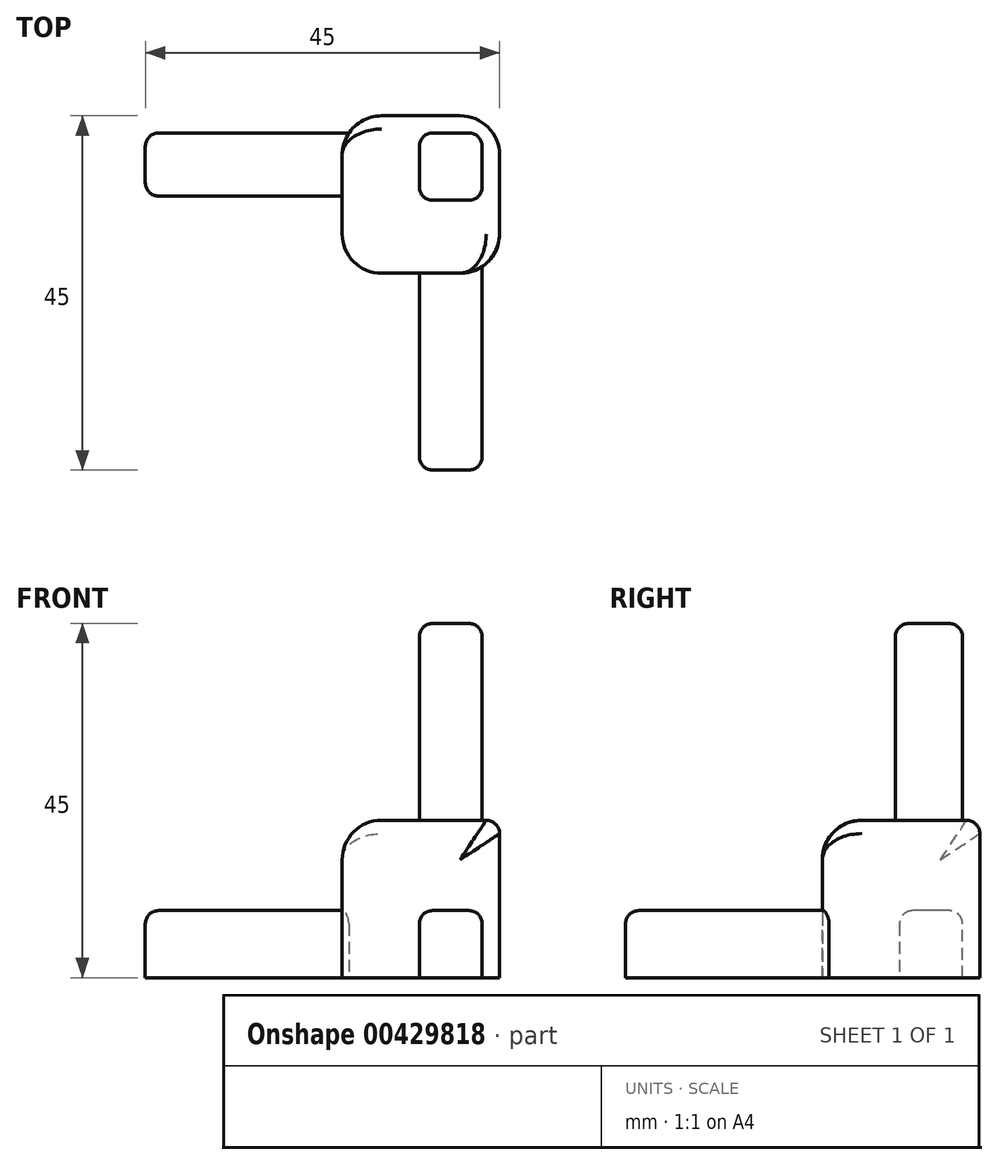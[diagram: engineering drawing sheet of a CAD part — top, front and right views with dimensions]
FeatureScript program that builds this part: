
annotation { "Feature Type Name" : "Feature", "Feature Type Description" : "" }
export const myFeature = defineFeature(function(context is Context, id is Id, definition is map)
    precondition{}
    {
        {
            var Q0;
            Q0=qCreatedBy(makeId("Front.planeOp"),FACE);
            var sketch = newSketch(context, id + "F0", { "sketchPlane" : qUnion([Q0])});
            skLineSegment(sketch, "E0.bottom", {"start": v(-6.86, 11.47) * mm, "end": v(13.14, 11.47) * mm});
            skLineSegment(sketch, "E0.top", {"start": v(-6.86, -8.53) * mm, "end": v(13.14, -8.53) * mm});
            skLineSegment(sketch, "E0.left", {"start": v(-6.86, 11.47) * mm, "end": v(-6.86, -8.53) * mm});
            skLineSegment(sketch, "E0.right", {"start": v(13.14, 11.47) * mm, "end": v(13.14, -8.53) * mm});
            skSolve(sketch);
        }
        {
            var Q0;
            Q0 = qSketchRegion(id + "F0", true);
            extrude(context, id + "F1", {"entities" : qUnion([Q0]), "depth" : 20 * mm});
        }
        {
            var Q0;
            Q0=makeQuery(id+"F1.opExtrude","SWEPT_FACE",FACE,{"disambiguationData":[OSD([sQuery(id+"F0.wireOp",EDGE,"E0.left")])]});
            var sketch = newSketch(context, id + "F2", { "sketchPlane" : qUnion([Q0])});
            skLineSegment(sketch, "E1", {"start": v(2.2, -8.53) * mm, "end": v(2.2, 0) * mm});
            skLineSegment(sketch, "E2", {"start": v(2.2, 0) * mm, "end": v(10.2, 0) * mm});
            skLineSegment(sketch, "E3", {"start": v(10.2, 0) * mm, "end": v(10.2, -8.53) * mm});
            skLineSegment(sketch, "E4", {"start": v(10.2, -8.53) * mm, "end": v(2.2, -8.53) * mm});
            skSolve(sketch);
        }
        {
            var Q0;
            Q0 = qSketchRegion(id + "F2", true);
            extrude(context, id + "F3", {"entities" : qUnion([Q0]), "operationType" : NewBodyOperationType.ADD, "depth" : 25 * mm});
        }
        {
            var Q0;
            Q0=makeQuery(id+"F1.opExtrude","CAP_FACE",FACE,{"disambiguationData":[OSD([sQuery(id+"F0.wireOp",EDGE,"E0.bottom"),sQuery(id+"F0.wireOp",EDGE,"E0.top"),sQuery(id+"F0.wireOp",EDGE,"E0.left"),sQuery(id+"F0.wireOp",EDGE,"E0.right")])],"isStart":false});
            var sketch = newSketch(context, id + "F4", { "sketchPlane" : qUnion([Q0])});
            skLineSegment(sketch, "E5.bottom", {"start": v(10.94, -8.53) * mm, "end": v(2.94, -8.53) * mm});
            skLineSegment(sketch, "E5.top", {"start": v(10.94, 0) * mm, "end": v(2.94, 0) * mm});
            skLineSegment(sketch, "E5.left", {"start": v(10.94, -8.53) * mm, "end": v(10.94, 0) * mm});
            skLineSegment(sketch, "E5.right", {"start": v(2.94, -8.53) * mm, "end": v(2.94, 0) * mm});
            skSolve(sketch);
        }
        {
            var Q0;
            Q0 = qSketchRegion(id + "F4", true);
            extrude(context, id + "F5", {"entities" : qUnion([Q0]), "operationType" : NewBodyOperationType.ADD, "depth" : 25 * mm});
        }
        {
            var Q0;
            Q0=makeQuery(id+"F1.opExtrude","SWEPT_FACE",FACE,{"disambiguationData":[OSD([sQuery(id+"F0.wireOp",EDGE,"E0.bottom")])]});
            var sketch = newSketch(context, id + "F6", { "sketchPlane" : qUnion([Q0])});
            skLineSegment(sketch, "E6", {"start": v(2.94, -2.2) * mm, "end": v(2.94, -10.73) * mm});
            skLineSegment(sketch, "E7", {"start": v(2.94, -10.73) * mm, "end": v(10.94, -10.73) * mm});
            skLineSegment(sketch, "E8", {"start": v(10.94, -10.73) * mm, "end": v(10.94, -2.2) * mm});
            skLineSegment(sketch, "E9", {"start": v(10.94, -2.2) * mm, "end": v(2.94, -2.2) * mm});
            skSolve(sketch);
        }
        {
            var Q0;
            Q0=makeQuery(id+"F6.imprint","IMPRINT",FACE,{"disambiguationData":[TD([[makeQuery(id+"F6.imprint","IMPRINT",EDGE,{"derivedFrom":sQuery(id+"F6.wireOp",EDGE,"E6")}),1.0]])]});
            extrude(context, id + "F7", {"entities" : qUnion([Q0]), "operationType" : NewBodyOperationType.ADD, "depth" : 25 * mm});
        }
        {
            var Q0;
            Q0=makeQuery(id+"F1.opExtrude","SWEPT_EDGE",EDGE,{"disambiguationData":[OSD([sQuery(id+"F0.wireOp",EDGE,"E0.bottom"),sQuery(id+"F0.wireOp",EDGE,"E0.left")])]});
            var Q1;
            Q1=makeQuery(id+"F1.opExtrude","CAP_EDGE",EDGE,{"disambiguationData":[OSD([sQuery(id+"F0.wireOp",EDGE,"E0.bottom")])],"isStart":false});
            var Q2;
            Q2=makeQuery(id+"F1.opExtrude","CAP_EDGE",EDGE,{"disambiguationData":[OSD([sQuery(id+"F0.wireOp",EDGE,"E0.left")])],"isStart":false});
            var Q3;
            Q3=makeQuery(id+"F1.opExtrude","CAP_EDGE",EDGE,{"disambiguationData":[OSD([sQuery(id+"F0.wireOp",EDGE,"E0.left")])],"isStart":true});
            var Q4;
            Q4=makeQuery(id+"F1.opExtrude","CAP_EDGE",EDGE,{"disambiguationData":[OSD([sQuery(id+"F0.wireOp",EDGE,"E0.right")])],"isStart":true});
            var Q5;
            Q5=makeQuery(id+"F1.opExtrude","CAP_EDGE",EDGE,{"disambiguationData":[OSD([sQuery(id+"F0.wireOp",EDGE,"E0.right")])],"isStart":false});
            fillet(context, id + "F8", {"entities" : qUnion([Q0, Q1, Q2, Q3, Q4, Q5]), "radius" : 5 * mm, "tangentPropagation" : true, "allowEdgeOverflow" : false});
        }
        {
            var Q0;
            Q0=makeQuery(id+"F3.opExtrude","CAP_EDGE",EDGE,{"disambiguationData":[OSD([sQuery(id+"F2.wireOp",EDGE,"E2")])],"isStart":false});
            var Q1;
            Q1=makeQuery(id+"F3.opExtrude","CAP_EDGE",EDGE,{"disambiguationData":[OSD([sQuery(id+"F2.wireOp",EDGE,"E3")])],"isStart":false});
            var Q2;
            Q2=makeQuery(id+"F3.opExtrude","SWEPT_EDGE",EDGE,{"disambiguationData":[OSD([sQuery(id+"F2.wireOp",EDGE,"E2"),sQuery(id+"F2.wireOp",EDGE,"E3")])]});
            var Q3;
            Q3=makeQuery(id+"F3.opExtrude","SWEPT_EDGE",EDGE,{"disambiguationData":[OSD([sQuery(id+"F2.wireOp",EDGE,"E1"),sQuery(id+"F2.wireOp",EDGE,"E2")])]});
            var Q4;
            Q4=makeQuery(id+"F5.opExtrude","SWEPT_EDGE",EDGE,{"disambiguationData":[OSD([sQuery(id+"F4.wireOp",EDGE,"E5.top"),sQuery(id+"F4.wireOp",EDGE,"E5.right")])]});
            var Q5;
            Q5=makeQuery(id+"F5.opExtrude","CAP_EDGE",EDGE,{"disambiguationData":[OSD([sQuery(id+"F4.wireOp",EDGE,"E5.right")])],"isStart":false});
            var Q6;
            Q6=makeQuery(id+"F5.opExtrude","CAP_EDGE",EDGE,{"disambiguationData":[OSD([sQuery(id+"F4.wireOp",EDGE,"E5.top")])],"isStart":false});
            var Q7;
            Q7=makeQuery(id+"F5.opExtrude","SWEPT_EDGE",EDGE,{"disambiguationData":[OSD([sQuery(id+"F4.wireOp",EDGE,"E5.top"),sQuery(id+"F4.wireOp",EDGE,"E5.left")])]});
            var Q8;
            Q8=makeQuery(id+"F3.opExtrude","CAP_EDGE",EDGE,{"disambiguationData":[OSD([sQuery(id+"F2.wireOp",EDGE,"E1")])],"isStart":false});
            var Q9;
            Q9=makeQuery(id+"F5.opExtrude","CAP_EDGE",EDGE,{"disambiguationData":[OSD([sQuery(id+"F4.wireOp",EDGE,"E5.left")])],"isStart":false});
            var Q10;
            Q10=makeQuery(id+"F7.opExtrude","SWEPT_EDGE",EDGE,{"disambiguationData":[OSD([sQuery(id+"F6.wireOp",EDGE,"E6"),sQuery(id+"F6.wireOp",EDGE,"E7")])]});
            var Q11;
            Q11=makeQuery(id+"F7.opExtrude","CAP_EDGE",EDGE,{"disambiguationData":[OSD([sQuery(id+"F6.wireOp",EDGE,"E6")])],"isStart":false});
            var Q12;
            Q12=makeQuery(id+"F7.opExtrude","CAP_EDGE",EDGE,{"disambiguationData":[OSD([sQuery(id+"F6.wireOp",EDGE,"E7")])],"isStart":false});
            var Q13;
            Q13=makeQuery(id+"F7.opExtrude","CAP_EDGE",EDGE,{"disambiguationData":[OSD([sQuery(id+"F6.wireOp",EDGE,"E9")])],"isStart":false});
            var Q14;
            Q14=makeQuery(id+"F7.opExtrude","CAP_EDGE",EDGE,{"disambiguationData":[OSD([sQuery(id+"F6.wireOp",EDGE,"E8")])],"isStart":false});
            var Q15;
            Q15=makeQuery(id+"F7.opExtrude","SWEPT_EDGE",EDGE,{"disambiguationData":[OSD([sQuery(id+"F6.wireOp",EDGE,"E8"),sQuery(id+"F6.wireOp",EDGE,"E9")])]});
            var Q16;
            Q16=makeQuery(id+"F1.opExtrude","CAP_EDGE",EDGE,{"disambiguationData":[OSD([sQuery(id+"F0.wireOp",EDGE,"E0.bottom")])],"isStart":true});
            var Q17;
            Q17=makeQuery(id+"F7.opExtrude","SWEPT_EDGE",EDGE,{"disambiguationData":[OSD([sQuery(id+"F6.wireOp",EDGE,"E6"),sQuery(id+"F6.wireOp",EDGE,"E9")])]});
            var Q18;
            Q18=makeQuery(id+"F7.opExtrude","SWEPT_EDGE",EDGE,{"disambiguationData":[OSD([sQuery(id+"F6.wireOp",EDGE,"E7"),sQuery(id+"F6.wireOp",EDGE,"E8")])]});
            fillet(context, id + "F9", {"entities" : qUnion([Q0, Q1, Q2, Q3, Q4, Q5, Q6, Q7, Q8, Q9, Q10, Q11, Q12, Q13, Q14, Q15, Q16, Q17, Q18]), "radius" : 1.69 * mm, "tangentPropagation" : true, "allowEdgeOverflow" : false});
        }
    });
